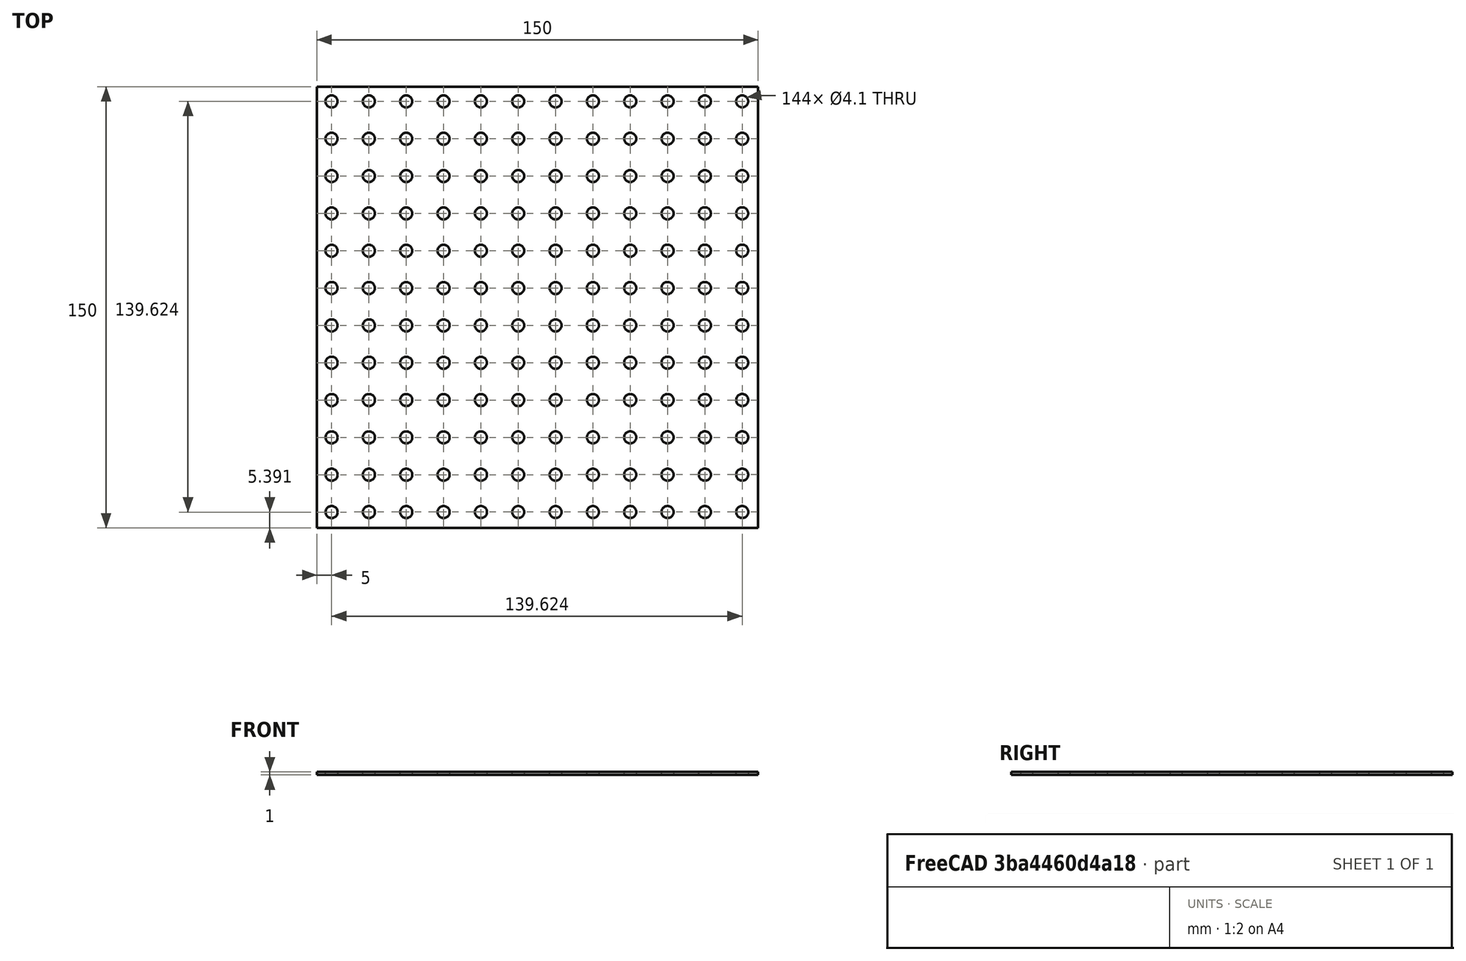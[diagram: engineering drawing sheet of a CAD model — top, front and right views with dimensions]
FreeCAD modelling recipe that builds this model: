
FCSTD DOCUMENT  (FreeCAD 0.18.3R)
Label: base_plate
License: All rights reserved
LicenseURL: http://en.wikipedia.org/wiki/All_rights_reserved
objects: Sketcher::SketchObject×2, PartDesign::Pad×1, PartDesign::Pocket×1, PartDesign::Body×1
note: 7 computed .brp shape members not serialized (recipe doc carries the construction recipe); baked Part::Feature solids carry a one-line shape summary decoded from their .brp

FEATURE [Sketcher::SketchObject] Sketch
  MapMode = 5
  Support = -> [XY_Plane]
  sketch-geometry (4):
    g0: LineSegment StartX=-75 StartY=75 StartZ=0 EndX=75 EndY=75 EndZ=0
    g1: LineSegment StartX=75 StartY=75 StartZ=0 EndX=75 EndY=-75 EndZ=0
    g2: LineSegment StartX=75 StartY=-75 StartZ=0 EndX=-75 EndY=-75 EndZ=0
    g3: LineSegment StartX=-75 StartY=-75 StartZ=0 EndX=-75 EndY=75 EndZ=0
  constraints (10):
    c: Coincident(g0,g1)
    c: Coincident(g1,g2)
    c: Coincident(g2,g3)
    c: Coincident(g3,g0)
    c: Horizontal(g0)
    c: Vertical(g3)
    c: Symmetric(g1,g0,g-1)
    c: Symmetric(g2,g1,g-2)
    c: Equal(g1,g0)
    c: DistanceY(g1,g1) = 150
FEATURE [PartDesign::Pad] Pad
  Length = 1
  Length2 = 100
  Profile = -> Sketch
  Type = 0
FEATURE [Sketcher::SketchObject] Sketch001
  ExternalGeometry = -> [Pad]
  MapMode = 5
  Placement = pos=(0,0,1) rot=(0,0,1;0rad)
  Support = -> [Pad]
  sketch-geometry (144):
    g0: Circle CenterX=-70 CenterY=70 CenterZ=0 NormalX=0 NormalY=0 NormalZ=1 AngleXU=0 Radius=2.05
    g1: Circle CenterX=-57.3083 CenterY=70.0014 CenterZ=0 NormalX=0 NormalY=0 NormalZ=1 AngleXU=0 Radius=2.05
    g2: Circle CenterX=-44.6165 CenterY=70.0027 CenterZ=0 NormalX=0 NormalY=0 NormalZ=1 AngleXU=0 Radius=2.05
    g3: Circle CenterX=-31.9248 CenterY=70.0041 CenterZ=0 NormalX=0 NormalY=0 NormalZ=1 AngleXU=0 Radius=2.05
    g4: Circle CenterX=-19.2331 CenterY=70.0054 CenterZ=0 NormalX=0 NormalY=0 NormalZ=1 AngleXU=0 Radius=2.05
    g5: Circle CenterX=-6.54135 CenterY=70.0067 CenterZ=0 NormalX=0 NormalY=0 NormalZ=1 AngleXU=0 Radius=2.05
    g6: Circle CenterX=6.15038 CenterY=70.0081 CenterZ=0 NormalX=0 NormalY=0 NormalZ=1 AngleXU=0 Radius=2.05
    g7: Circle CenterX=18.8421 CenterY=70.0095 CenterZ=0 NormalX=0 NormalY=0 NormalZ=1 AngleXU=0 Radius=2.05
    g8: Circle CenterX=31.5338 CenterY=70.0108 CenterZ=0 NormalX=0 NormalY=0 NormalZ=1 AngleXU=0 Radius=2.05
    g9: Circle CenterX=44.2256 CenterY=70.0122 CenterZ=0 NormalX=0 NormalY=0 NormalZ=1 AngleXU=0 Radius=2.05
    g10: Circle CenterX=56.9173 CenterY=70.0135 CenterZ=0 NormalX=0 NormalY=0 NormalZ=1 AngleXU=0 Radius=2.05
    g11: Circle CenterX=69.609 CenterY=70.0148 CenterZ=0 NormalX=0 NormalY=0 NormalZ=1 AngleXU=0 Radius=2.05
    g12: Circle CenterX=-69.9986 CenterY=57.3083 CenterZ=0 NormalX=0 NormalY=0 NormalZ=1 AngleXU=0 Radius=2.05
    g13: Circle CenterX=-57.3069 CenterY=57.3096 CenterZ=0 NormalX=0 NormalY=0 NormalZ=1 AngleXU=0 Radius=2.05
    g14: Circle CenterX=-44.6152 CenterY=57.311 CenterZ=0 NormalX=0 NormalY=0 NormalZ=1 AngleXU=0 Radius=2.05
    g15: Circle CenterX=-31.9235 CenterY=57.3123 CenterZ=0 NormalX=0 NormalY=0 NormalZ=1 AngleXU=0 Radius=2.05
    g16: Circle CenterX=-19.2317 CenterY=57.3137 CenterZ=0 NormalX=0 NormalY=0 NormalZ=1 AngleXU=0 Radius=2.05
    g17: Circle CenterX=-6.54 CenterY=57.315 CenterZ=0 NormalX=0 NormalY=0 NormalZ=1 AngleXU=0 Radius=2.05
    g18: Circle CenterX=6.15173 CenterY=57.3164 CenterZ=0 NormalX=0 NormalY=0 NormalZ=1 AngleXU=0 Radius=2.05
    g19: Circle CenterX=18.8435 CenterY=57.3177 CenterZ=0 NormalX=0 NormalY=0 NormalZ=1 AngleXU=0 Radius=2.05
    g20: Circle CenterX=31.5352 CenterY=57.3191 CenterZ=0 NormalX=0 NormalY=0 NormalZ=1 AngleXU=0 Radius=2.05
    g21: Circle CenterX=44.2269 CenterY=57.3204 CenterZ=0 NormalX=0 NormalY=0 NormalZ=1 AngleXU=0 Radius=2.05
    g22: Circle CenterX=56.9187 CenterY=57.3218 CenterZ=0 NormalX=0 NormalY=0 NormalZ=1 AngleXU=0 Radius=2.05
    g23: Circle CenterX=69.6104 CenterY=57.3231 CenterZ=0 NormalX=0 NormalY=0 NormalZ=1 AngleXU=0 Radius=2.05
    g24: Circle CenterX=-69.9973 CenterY=44.6165 CenterZ=0 NormalX=0 NormalY=0 NormalZ=1 AngleXU=0 Radius=2.05
    g25: Circle CenterX=-57.3056 CenterY=44.6179 CenterZ=0 NormalX=0 NormalY=0 NormalZ=1 AngleXU=0 Radius=2.05
    g26: Circle CenterX=-44.6138 CenterY=44.6192 CenterZ=0 NormalX=0 NormalY=0 NormalZ=1 AngleXU=0 Radius=2.05
    g27: Circle CenterX=-31.9221 CenterY=44.6206 CenterZ=0 NormalX=0 NormalY=0 NormalZ=1 AngleXU=0 Radius=2.05
    g28: Circle CenterX=-19.2304 CenterY=44.6219 CenterZ=0 NormalX=0 NormalY=0 NormalZ=1 AngleXU=0 Radius=2.05
    g29: Circle CenterX=-6.53865 CenterY=44.6233 CenterZ=0 NormalX=0 NormalY=0 NormalZ=1 AngleXU=0 Radius=2.05
    g30: Circle CenterX=6.15308 CenterY=44.6246 CenterZ=0 NormalX=0 NormalY=0 NormalZ=1 AngleXU=0 Radius=2.05
    g31: Circle CenterX=18.8448 CenterY=44.626 CenterZ=0 NormalX=0 NormalY=0 NormalZ=1 AngleXU=0 Radius=2.05
    g32: Circle CenterX=31.5365 CenterY=44.6273 CenterZ=0 NormalX=0 NormalY=0 NormalZ=1 AngleXU=0 Radius=2.05
    g33: Circle CenterX=44.2283 CenterY=44.6287 CenterZ=0 NormalX=0 NormalY=0 NormalZ=1 AngleXU=0 Radius=2.05
    g34: Circle CenterX=56.92 CenterY=44.63 CenterZ=0 NormalX=0 NormalY=0 NormalZ=1 AngleXU=0 Radius=2.05
    g35: Circle CenterX=69.6117 CenterY=44.6314 CenterZ=0 NormalX=0 NormalY=0 NormalZ=1 AngleXU=0 Radius=2.05
    g36: Circle CenterX=-69.9959 CenterY=31.9248 CenterZ=0 NormalX=0 NormalY=0 NormalZ=1 AngleXU=0 Radius=2.05
    g37: Circle CenterX=-57.3042 CenterY=31.9262 CenterZ=0 NormalX=0 NormalY=0 NormalZ=1 AngleXU=0 Radius=2.05
    g38: Circle CenterX=-44.6125 CenterY=31.9275 CenterZ=0 NormalX=0 NormalY=0 NormalZ=1 AngleXU=0 Radius=2.05
    g39: Circle CenterX=-31.9208 CenterY=31.9289 CenterZ=0 NormalX=0 NormalY=0 NormalZ=1 AngleXU=0 Radius=2.05
    g40: Circle CenterX=-19.229 CenterY=31.9302 CenterZ=0 NormalX=0 NormalY=0 NormalZ=1 AngleXU=0 Radius=2.05
    g41: Circle CenterX=-6.5373 CenterY=31.9316 CenterZ=0 NormalX=0 NormalY=0 NormalZ=1 AngleXU=0 Radius=2.05
    g42: Circle CenterX=6.15443 CenterY=31.9329 CenterZ=0 NormalX=0 NormalY=0 NormalZ=1 AngleXU=0 Radius=2.05
    g43: Circle CenterX=18.8462 CenterY=31.9343 CenterZ=0 NormalX=0 NormalY=0 NormalZ=1 AngleXU=0 Radius=2.05
    g44: Circle CenterX=31.5379 CenterY=31.9356 CenterZ=0 NormalX=0 NormalY=0 NormalZ=1 AngleXU=0 Radius=2.05
    g45: Circle CenterX=44.2296 CenterY=31.937 CenterZ=0 NormalX=0 NormalY=0 NormalZ=1 AngleXU=0 Radius=2.05
    g46: Circle CenterX=56.9214 CenterY=31.9383 CenterZ=0 NormalX=0 NormalY=0 NormalZ=1 AngleXU=0 Radius=2.05
    g47: Circle CenterX=69.6131 CenterY=31.9397 CenterZ=0 NormalX=0 NormalY=0 NormalZ=1 AngleXU=0 Radius=2.05
    g48: Circle CenterX=-69.9946 CenterY=19.2331 CenterZ=0 NormalX=0 NormalY=0 NormalZ=1 AngleXU=0 Radius=2.05
    g49: Circle CenterX=-57.3029 CenterY=19.2344 CenterZ=0 NormalX=0 NormalY=0 NormalZ=1 AngleXU=0 Radius=2.05
    g50: Circle CenterX=-44.6111 CenterY=19.2358 CenterZ=0 NormalX=0 NormalY=0 NormalZ=1 AngleXU=0 Radius=2.05
    g51: Circle CenterX=-31.9194 CenterY=19.2371 CenterZ=0 NormalX=0 NormalY=0 NormalZ=1 AngleXU=0 Radius=2.05
    g52: Circle CenterX=-19.2277 CenterY=19.2385 CenterZ=0 NormalX=0 NormalY=0 NormalZ=1 AngleXU=0 Radius=2.05
    g53: Circle CenterX=-6.53595 CenterY=19.2398 CenterZ=0 NormalX=0 NormalY=0 NormalZ=1 AngleXU=0 Radius=2.05
    g54: Circle CenterX=6.15578 CenterY=19.2412 CenterZ=0 NormalX=0 NormalY=0 NormalZ=1 AngleXU=0 Radius=2.05
    g55: Circle CenterX=18.8475 CenterY=19.2425 CenterZ=0 NormalX=0 NormalY=0 NormalZ=1 AngleXU=0 Radius=2.05
    g56: Circle CenterX=31.5392 CenterY=19.2439 CenterZ=0 NormalX=0 NormalY=0 NormalZ=1 AngleXU=0 Radius=2.05
    g57: Circle CenterX=44.231 CenterY=19.2452 CenterZ=0 NormalX=0 NormalY=0 NormalZ=1 AngleXU=0 Radius=2.05
    g58: Circle CenterX=56.9227 CenterY=19.2466 CenterZ=0 NormalX=0 NormalY=0 NormalZ=1 AngleXU=0 Radius=2.05
    g59: Circle CenterX=69.6144 CenterY=19.2479 CenterZ=0 NormalX=0 NormalY=0 NormalZ=1 AngleXU=0 Radius=2.05
    g60: Circle CenterX=-69.9932 CenterY=6.54135 CenterZ=0 NormalX=0 NormalY=0 NormalZ=1 AngleXU=0 Radius=2.05
    g61: Circle CenterX=-57.3015 CenterY=6.5427 CenterZ=0 NormalX=0 NormalY=0 NormalZ=1 AngleXU=0 Radius=2.05
    g62: Circle CenterX=-44.6098 CenterY=6.54405 CenterZ=0 NormalX=0 NormalY=0 NormalZ=1 AngleXU=0 Radius=2.05
    g63: Circle CenterX=-31.9181 CenterY=6.5454 CenterZ=0 NormalX=0 NormalY=0 NormalZ=1 AngleXU=0 Radius=2.05
    g64: Circle CenterX=-19.2263 CenterY=6.54675 CenterZ=0 NormalX=0 NormalY=0 NormalZ=1 AngleXU=0 Radius=2.05
    g65: Circle CenterX=-6.5346 CenterY=6.5481 CenterZ=0 NormalX=0 NormalY=0 NormalZ=1 AngleXU=0 Radius=2.05
    g66: Circle CenterX=6.15713 CenterY=6.54945 CenterZ=0 NormalX=0 NormalY=0 NormalZ=1 AngleXU=0 Radius=2.05
    g67: Circle CenterX=18.8489 CenterY=6.5508 CenterZ=0 NormalX=0 NormalY=0 NormalZ=1 AngleXU=0 Radius=2.05
    g68: Circle CenterX=31.5406 CenterY=6.55215 CenterZ=0 NormalX=0 NormalY=0 NormalZ=1 AngleXU=0 Radius=2.05
    g69: Circle CenterX=44.2323 CenterY=6.5535 CenterZ=0 NormalX=0 NormalY=0 NormalZ=1 AngleXU=0 Radius=2.05
    g70: Circle CenterX=56.9241 CenterY=6.55485 CenterZ=0 NormalX=0 NormalY=0 NormalZ=1 AngleXU=0 Radius=2.05
    g71: Circle CenterX=69.6158 CenterY=6.5562 CenterZ=0 NormalX=0 NormalY=0 NormalZ=1 AngleXU=0 Radius=2.05
    g72: Circle CenterX=-69.9919 CenterY=-6.15038 CenterZ=0 NormalX=0 NormalY=0 NormalZ=1 AngleXU=0 Radius=2.05
    g73: Circle CenterX=-57.3002 CenterY=-6.14903 CenterZ=0 NormalX=0 NormalY=0 NormalZ=1 AngleXU=0 Radius=2.05
    g74: Circle CenterX=-44.6084 CenterY=-6.14768 CenterZ=0 NormalX=0 NormalY=0 NormalZ=1 AngleXU=0 Radius=2.05
    g75: Circle CenterX=-31.9167 CenterY=-6.14633 CenterZ=0 NormalX=0 NormalY=0 NormalZ=1 AngleXU=0 Radius=2.05
    g76: Circle CenterX=-19.225 CenterY=-6.14498 CenterZ=0 NormalX=0 NormalY=0 NormalZ=1 AngleXU=0 Radius=2.05
    g77: Circle CenterX=-6.53325 CenterY=-6.14363 CenterZ=0 NormalX=0 NormalY=0 NormalZ=1 AngleXU=0 Radius=2.05
    g78: Circle CenterX=6.15848 CenterY=-6.14228 CenterZ=0 NormalX=0 NormalY=0 NormalZ=1 AngleXU=0 Radius=2.05
    g79: Circle CenterX=18.8502 CenterY=-6.14093 CenterZ=0 NormalX=0 NormalY=0 NormalZ=1 AngleXU=0 Radius=2.05
    g80: Circle CenterX=31.5419 CenterY=-6.13958 CenterZ=0 NormalX=0 NormalY=0 NormalZ=1 AngleXU=0 Radius=2.05
    g81: Circle CenterX=44.2337 CenterY=-6.13823 CenterZ=0 NormalX=0 NormalY=0 NormalZ=1 AngleXU=0 Radius=2.05
    g82: Circle CenterX=56.9254 CenterY=-6.13688 CenterZ=0 NormalX=0 NormalY=0 NormalZ=1 AngleXU=0 Radius=2.05
    g83: Circle CenterX=69.6171 CenterY=-6.13553 CenterZ=0 NormalX=0 NormalY=0 NormalZ=1 AngleXU=0 Radius=2.05
    g84: Circle CenterX=-69.9905 CenterY=-18.8421 CenterZ=0 NormalX=0 NormalY=0 NormalZ=1 AngleXU=0 Radius=2.05
    g85: Circle CenterX=-57.2988 CenterY=-18.8408 CenterZ=0 NormalX=0 NormalY=0 NormalZ=1 AngleXU=0 Radius=2.05
    g86: Circle CenterX=-44.6071 CenterY=-18.8394 CenterZ=0 NormalX=0 NormalY=0 NormalZ=1 AngleXU=0 Radius=2.05
    g87: Circle CenterX=-31.9154 CenterY=-18.8381 CenterZ=0 NormalX=0 NormalY=0 NormalZ=1 AngleXU=0 Radius=2.05
    g88: Circle CenterX=-19.2236 CenterY=-18.8367 CenterZ=0 NormalX=0 NormalY=0 NormalZ=1 AngleXU=0 Radius=2.05
    g89: Circle CenterX=-6.5319 CenterY=-18.8354 CenterZ=0 NormalX=0 NormalY=0 NormalZ=1 AngleXU=0 Radius=2.05
    g90: Circle CenterX=6.15983 CenterY=-18.834 CenterZ=0 NormalX=0 NormalY=0 NormalZ=1 AngleXU=0 Radius=2.05
    g91: Circle CenterX=18.8516 CenterY=-18.8327 CenterZ=0 NormalX=0 NormalY=0 NormalZ=1 AngleXU=0 Radius=2.05
    g92: Circle CenterX=31.5433 CenterY=-18.8313 CenterZ=0 NormalX=0 NormalY=0 NormalZ=1 AngleXU=0 Radius=2.05
    g93: Circle CenterX=44.235 CenterY=-18.83 CenterZ=0 NormalX=0 NormalY=0 NormalZ=1 AngleXU=0 Radius=2.05
    g94: Circle CenterX=56.9268 CenterY=-18.8286 CenterZ=0 NormalX=0 NormalY=0 NormalZ=1 AngleXU=0 Radius=2.05
    g95: Circle CenterX=69.6185 CenterY=-18.8273 CenterZ=0 NormalX=0 NormalY=0 NormalZ=1 AngleXU=0 Radius=2.05
    g96: Circle CenterX=-69.9892 CenterY=-31.5338 CenterZ=0 NormalX=0 NormalY=0 NormalZ=1 AngleXU=0 Radius=2.05
    g97: Circle CenterX=-57.2975 CenterY=-31.5325 CenterZ=0 NormalX=0 NormalY=0 NormalZ=1 AngleXU=0 Radius=2.05
    g98: Circle CenterX=-44.6057 CenterY=-31.5311 CenterZ=0 NormalX=0 NormalY=0 NormalZ=1 AngleXU=0 Radius=2.05
    g99: Circle CenterX=-31.914 CenterY=-31.5298 CenterZ=0 NormalX=0 NormalY=0 NormalZ=1 AngleXU=0 Radius=2.05
    g100: Circle CenterX=-19.2223 CenterY=-31.5284 CenterZ=0 NormalX=0 NormalY=0 NormalZ=1 AngleXU=0 Radius=2.05
    g101: Circle CenterX=-6.53055 CenterY=-31.5271 CenterZ=0 NormalX=0 NormalY=0 NormalZ=1 AngleXU=0 Radius=2.05
    g102: Circle CenterX=6.16118 CenterY=-31.5257 CenterZ=0 NormalX=0 NormalY=0 NormalZ=1 AngleXU=0 Radius=2.05
    g103: Circle CenterX=18.8529 CenterY=-31.5244 CenterZ=0 NormalX=0 NormalY=0 NormalZ=1 AngleXU=0 Radius=2.05
    g104: Circle CenterX=31.5446 CenterY=-31.523 CenterZ=0 NormalX=0 NormalY=0 NormalZ=1 AngleXU=0 Radius=2.05
    g105: Circle CenterX=44.2364 CenterY=-31.5217 CenterZ=0 NormalX=0 NormalY=0 NormalZ=1 AngleXU=0 Radius=2.05
    g106: Circle CenterX=56.9281 CenterY=-31.5203 CenterZ=0 NormalX=0 NormalY=0 NormalZ=1 AngleXU=0 Radius=2.05
    g107: Circle CenterX=69.6198 CenterY=-31.519 CenterZ=0 NormalX=0 NormalY=0 NormalZ=1 AngleXU=0 Radius=2.05
    g108: Circle CenterX=-69.9878 CenterY=-44.2256 CenterZ=0 NormalX=0 NormalY=0 NormalZ=1 AngleXU=0 Radius=2.05
    g109: Circle CenterX=-57.2961 CenterY=-44.2242 CenterZ=0 NormalX=0 NormalY=0 NormalZ=1 AngleXU=0 Radius=2.05
    g110: Circle CenterX=-44.6044 CenterY=-44.2229 CenterZ=0 NormalX=0 NormalY=0 NormalZ=1 AngleXU=0 Radius=2.05
    g111: Circle CenterX=-31.9127 CenterY=-44.2215 CenterZ=0 NormalX=0 NormalY=0 NormalZ=1 AngleXU=0 Radius=2.05
    g112: Circle CenterX=-19.2209 CenterY=-44.2202 CenterZ=0 NormalX=0 NormalY=0 NormalZ=1 AngleXU=0 Radius=2.05
    g113: Circle CenterX=-6.5292 CenterY=-44.2188 CenterZ=0 NormalX=0 NormalY=0 NormalZ=1 AngleXU=0 Radius=2.05
    g114: Circle CenterX=6.16253 CenterY=-44.2175 CenterZ=0 NormalX=0 NormalY=0 NormalZ=1 AngleXU=0 Radius=2.05
    g115: Circle CenterX=18.8543 CenterY=-44.2161 CenterZ=0 NormalX=0 NormalY=0 NormalZ=1 AngleXU=0 Radius=2.05
    g116: Circle CenterX=31.546 CenterY=-44.2148 CenterZ=0 NormalX=0 NormalY=0 NormalZ=1 AngleXU=0 Radius=2.05
    g117: Circle CenterX=44.2377 CenterY=-44.2134 CenterZ=0 NormalX=0 NormalY=0 NormalZ=1 AngleXU=0 Radius=2.05
    g118: Circle CenterX=56.9295 CenterY=-44.2121 CenterZ=0 NormalX=0 NormalY=0 NormalZ=1 AngleXU=0 Radius=2.05
    g119: Circle CenterX=69.6212 CenterY=-44.2107 CenterZ=0 NormalX=0 NormalY=0 NormalZ=1 AngleXU=0 Radius=2.05
    g120: Circle CenterX=-69.9865 CenterY=-56.9173 CenterZ=0 NormalX=0 NormalY=0 NormalZ=1 AngleXU=0 Radius=2.05
    g121: Circle CenterX=-57.2948 CenterY=-56.9159 CenterZ=0 NormalX=0 NormalY=0 NormalZ=1 AngleXU=0 Radius=2.05
    g122: Circle CenterX=-44.603 CenterY=-56.9146 CenterZ=0 NormalX=0 NormalY=0 NormalZ=1 AngleXU=0 Radius=2.05
    g123: Circle CenterX=-31.9113 CenterY=-56.9132 CenterZ=0 NormalX=0 NormalY=0 NormalZ=1 AngleXU=0 Radius=2.05
    g124: Circle CenterX=-19.2196 CenterY=-56.9119 CenterZ=0 NormalX=0 NormalY=0 NormalZ=1 AngleXU=0 Radius=2.05
    g125: Circle CenterX=-6.52785 CenterY=-56.9106 CenterZ=0 NormalX=0 NormalY=0 NormalZ=1 AngleXU=0 Radius=2.05
    g126: Circle CenterX=6.16388 CenterY=-56.9092 CenterZ=0 NormalX=0 NormalY=0 NormalZ=1 AngleXU=0 Radius=2.05
    g127: Circle CenterX=18.8556 CenterY=-56.9078 CenterZ=0 NormalX=0 NormalY=0 NormalZ=1 AngleXU=0 Radius=2.05
    g128: Circle CenterX=31.5473 CenterY=-56.9065 CenterZ=0 NormalX=0 NormalY=0 NormalZ=1 AngleXU=0 Radius=2.05
    g129: Circle CenterX=44.2391 CenterY=-56.9051 CenterZ=0 NormalX=0 NormalY=0 NormalZ=1 AngleXU=0 Radius=2.05
    g130: Circle CenterX=56.9308 CenterY=-56.9038 CenterZ=0 NormalX=0 NormalY=0 NormalZ=1 AngleXU=0 Radius=2.05
    g131: Circle CenterX=69.6225 CenterY=-56.9025 CenterZ=0 NormalX=0 NormalY=0 NormalZ=1 AngleXU=0 Radius=2.05
    g132: Circle CenterX=-69.9851 CenterY=-69.609 CenterZ=0 NormalX=0 NormalY=0 NormalZ=1 AngleXU=0 Radius=2.05
    g133: Circle CenterX=-57.2934 CenterY=-69.6077 CenterZ=0 NormalX=0 NormalY=0 NormalZ=1 AngleXU=0 Radius=2.05
    g134: Circle CenterX=-44.6017 CenterY=-69.6063 CenterZ=0 NormalX=0 NormalY=0 NormalZ=1 AngleXU=0 Radius=2.05
    g135: Circle CenterX=-31.91 CenterY=-69.605 CenterZ=0 NormalX=0 NormalY=0 NormalZ=1 AngleXU=0 Radius=2.05
    g136: Circle CenterX=-19.2182 CenterY=-69.6036 CenterZ=0 NormalX=0 NormalY=0 NormalZ=1 AngleXU=0 Radius=2.05
    g137: Circle CenterX=-6.5265 CenterY=-69.6023 CenterZ=0 NormalX=0 NormalY=0 NormalZ=1 AngleXU=0 Radius=2.05
    g138: Circle CenterX=6.16523 CenterY=-69.6009 CenterZ=0 NormalX=0 NormalY=0 NormalZ=1 AngleXU=0 Radius=2.05
    g139: Circle CenterX=18.857 CenterY=-69.5996 CenterZ=0 NormalX=0 NormalY=0 NormalZ=1 AngleXU=0 Radius=2.05
    g140: Circle CenterX=31.5487 CenterY=-69.5982 CenterZ=0 NormalX=0 NormalY=0 NormalZ=1 AngleXU=0 Radius=2.05
    g141: Circle CenterX=44.2404 CenterY=-69.5969 CenterZ=0 NormalX=0 NormalY=0 NormalZ=1 AngleXU=0 Radius=2.05
    g142: Circle CenterX=56.9322 CenterY=-69.5955 CenterZ=0 NormalX=0 NormalY=0 NormalZ=1 AngleXU=0 Radius=2.05
    g143: Circle CenterX=69.6239 CenterY=-69.5942 CenterZ=0 NormalX=0 NormalY=0 NormalZ=1 AngleXU=0 Radius=2.05
  constraints (146):
    c: Radius(g0) = 2.05
    c: DistanceY(g0,g-6) = 5
    c: DistanceX(g-6,g0) = 5
    c: Equal(g0,g1) = 4.1
    c: Equal(g0,g2) = 4.1
    c: Equal(g0,g3) = 4.1
    c: Equal(g0,g4) = 4.1
    c: Equal(g0,g5) = 4.1
    c: Equal(g0,g6) = 4.1
    c: Equal(g0,g7) = 4.1
    c: Equal(g0,g8) = 4.1
    c: Equal(g0,g9) = 4.1
    c: Equal(g0,g10) = 4.1
    c: Equal(g0,g11) = 4.1
    c: Equal(g0,g12) = 4.1
    c: Equal(g0,g13) = 4.1
    c: Equal(g0,g14) = 4.1
    c: Equal(g0,g15) = 4.1
    c: Equal(g0,g16) = 4.1
    c: Equal(g0,g17) = 4.1
    c: Equal(g0,g18) = 4.1
    c: Equal(g0,g19) = 4.1
    c: Equal(g0,g20) = 4.1
    c: Equal(g0,g21) = 4.1
    c: Equal(g0,g22) = 4.1
    c: Equal(g0,g23) = 4.1
    c: Equal(g0,g24) = 4.1
    c: Equal(g0,g25) = 4.1
    c: Equal(g0,g26) = 4.1
    c: Equal(g0,g27) = 4.1
    c: Equal(g0,g28) = 4.1
    c: Equal(g0,g29) = 4.1
    c: Equal(g0,g30) = 4.1
    c: Equal(g0,g31) = 4.1
    c: Equal(g0,g32) = 4.1
    c: Equal(g0,g33) = 4.1
    c: Equal(g0,g34) = 4.1
    c: Equal(g0,g35) = 4.1
    c: Equal(g0,g36) = 4.1
    c: Equal(g0,g37) = 4.1
    c: Equal(g0,g38) = 4.1
    c: Equal(g0,g39) = 4.1
    c: Equal(g0,g40) = 4.1
    c: Equal(g0,g41) = 4.1
    c: Equal(g0,g42) = 4.1
    c: Equal(g0,g43) = 4.1
    c: Equal(g0,g44) = 4.1
    c: Equal(g0,g45) = 4.1
    c: Equal(g0,g46) = 4.1
    c: Equal(g0,g47) = 4.1
    c: Equal(g0,g48) = 4.1
    c: Equal(g0,g49) = 4.1
    c: Equal(g0,g50) = 4.1
    c: Equal(g0,g51) = 4.1
    c: Equal(g0,g52) = 4.1
    c: Equal(g0,g53) = 4.1
    c: Equal(g0,g54) = 4.1
    c: Equal(g0,g55) = 4.1
    c: Equal(g0,g56) = 4.1
    c: Equal(g0,g57) = 4.1
    c: Equal(g0,g58) = 4.1
    c: Equal(g0,g59) = 4.1
    c: Equal(g0,g60) = 4.1
    c: Equal(g0,g61) = 4.1
    c: Equal(g0,g62) = 4.1
    c: Equal(g0,g63) = 4.1
    c: Equal(g0,g64) = 4.1
    c: Equal(g0,g65) = 4.1
    c: Equal(g0,g66) = 4.1
    c: Equal(g0,g67) = 4.1
    c: Equal(g0,g68) = 4.1
    c: Equal(g0,g69) = 4.1
    c: Equal(g0,g70) = 4.1
    c: Equal(g0,g71) = 4.1
    c: Equal(g0,g72) = 4.1
    c: Equal(g0,g73) = 4.1
    c: Equal(g0,g74) = 4.1
    c: Equal(g0,g75) = 4.1
    c: Equal(g0,g76) = 4.1
    c: Equal(g0,g77) = 4.1
    c: Equal(g0,g78) = 4.1
    c: Equal(g0,g79) = 4.1
    c: Equal(g0,g80) = 4.1
    c: Equal(g0,g81) = 4.1
    c: Equal(g0,g82) = 4.1
    c: Equal(g0,g83) = 4.1
    c: Equal(g0,g84) = 4.1
    c: Equal(g0,g85) = 4.1
    c: Equal(g0,g86) = 4.1
    c: Equal(g0,g87) = 4.1
    c: Equal(g0,g88) = 4.1
    c: Equal(g0,g89) = 4.1
    c: Equal(g0,g90) = 4.1
    c: Equal(g0,g91) = 4.1
    c: Equal(g0,g92) = 4.1
    c: Equal(g0,g93) = 4.1
    c: Equal(g0,g94) = 4.1
    c: Equal(g0,g95) = 4.1
    c: Equal(g0,g96) = 4.1
    c: Equal(g0,g97) = 4.1
    c: Equal(g0,g98) = 4.1
    c: Equal(g0,g99) = 4.1
    c: Equal(g0,g100) = 4.1
    c: Equal(g0,g101) = 4.1
    c: Equal(g0,g102) = 4.1
    c: Equal(g0,g103) = 4.1
    c: Equal(g0,g104) = 4.1
    c: Equal(g0,g105) = 4.1
    c: Equal(g0,g106) = 4.1
    c: Equal(g0,g107) = 4.1
    c: Equal(g0,g108) = 4.1
    c: Equal(g0,g109) = 4.1
    c: Equal(g0,g110) = 4.1
    c: Equal(g0,g111) = 4.1
    c: Equal(g0,g112) = 4.1
    c: Equal(g0,g113) = 4.1
    c: Equal(g0,g114) = 4.1
    c: Equal(g0,g115) = 4.1
    c: Equal(g0,g116) = 4.1
    c: Equal(g0,g117) = 4.1
    c: Equal(g0,g118) = 4.1
    c: Equal(g0,g119) = 4.1
    c: Equal(g0,g120) = 4.1
    c: Equal(g0,g121) = 4.1
    c: Equal(g0,g122) = 4.1
    c: Equal(g0,g123) = 4.1
    c: Equal(g0,g124) = 4.1
    c: Equal(g0,g125) = 4.1
    c: Equal(g0,g126) = 4.1
    c: Equal(g0,g127) = 4.1
    c: Equal(g0,g128) = 4.1
    c: Equal(g0,g129) = 4.1
    c: Equal(g0,g130) = 4.1
    c: Equal(g0,g131) = 4.1
    c: Equal(g0,g132) = 4.1
    c: Equal(g0,g133) = 4.1
    c: Equal(g0,g134) = 4.1
    c: Equal(g0,g135) = 4.1
    c: Equal(g0,g136) = 4.1
    c: Equal(g0,g137) = 4.1
    c: Equal(g0,g138) = 4.1
    c: Equal(g0,g139) = 4.1
    c: Equal(g0,g140) = 4.1
    c: Equal(g0,g141) = 4.1
    c: Equal(g0,g142) = 4.1
    c: Equal(g0,g143) = 4.1
FEATURE [PartDesign::Pocket] Pocket
  BaseFeature = -> Pad
  Length = 5
  Length2 = 100
  Profile = -> Sketch001
  Type = 1
FEATURE [PartDesign::Body] Body
  Group = -> [Sketch,Pad,Sketch001,Pocket]
  Origin = -> Origin
  Tip = -> Pocket
